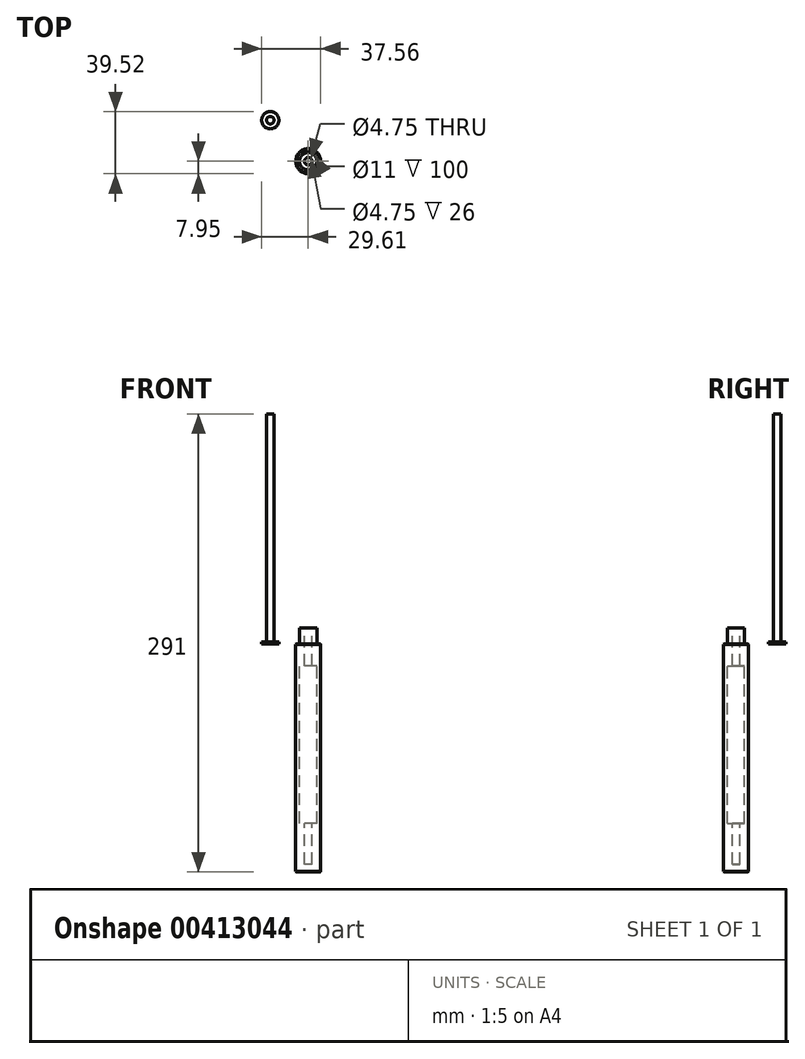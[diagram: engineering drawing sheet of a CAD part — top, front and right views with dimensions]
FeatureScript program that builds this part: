
annotation { "Feature Type Name" : "Feature", "Feature Type Description" : "" }
export const myFeature = defineFeature(function(context is Context, id is Id, definition is map)
    precondition{}
    {
        {
            var Q0;
            Q0=qCreatedBy(makeId("Top.planeOp"),FACE);
            var sketch = newSketch(context, id + "F0", { "sketchPlane" : qUnion([Q0])});
            skCircle(sketch, "E0", {"center": v(0, 0) * mm, "radius": 7.95 * mm});
            skSolve(sketch);
        }
        {
            var Q0;
            Q0=makeQuery(id+"F0.imprint","IMPRINT",FACE,{"disambiguationData":[TD([[makeQuery(id+"F0.imprint","IMPRINT",EDGE,{"derivedFrom":sQuery(id+"F0.wireOp",EDGE,"E0")}),1.0]])]});
            extrude(context, id + "F1", {"entities" : qUnion([Q0]), "oppositeDirection" : true, "depth" : 145 * mm});
        }
        {
            var Q0;
            Q0=makeQuery(id+"F1.opExtrude","CAP_FACE",FACE,{"disambiguationData":[OSD([sQuery(id+"F0.wireOp",EDGE,"E0")])],"isStart":true});
            var sketch = newSketch(context, id + "F2", { "sketchPlane" : qUnion([Q0])});
            skCircle(sketch, "E1", {"center": v(0, 0) * mm, "radius": 5.5 * mm});
            skSolve(sketch);
        }
        {
            var Q0;
            Q0=makeQuery(id+"F2.imprint","IMPRINT",FACE,{"disambiguationData":[TD([[makeQuery(id+"F2.imprint","IMPRINT",EDGE,{"derivedFrom":sQuery(id+"F2.wireOp",EDGE,"E1")}),1.0]])]});
            extrude(context, id + "F3", {"entities" : qUnion([Q0]), "operationType" : NewBodyOperationType.ADD, "depth" : 10 * mm});
        }
        {
            var Q0;
            Q0=makeQuery(id+"F1.opExtrude","CAP_EDGE",EDGE,{"disambiguationData":[OSD([sQuery(id+"F0.wireOp",EDGE,"E0")])],"isStart":true});
            var Q1;
            Q1=makeQuery(id+"F1.opExtrude","CAP_EDGE",EDGE,{"disambiguationData":[OSD([sQuery(id+"F0.wireOp",EDGE,"E0")])],"isStart":false});
            chamfer(context, id + "F4", {"entities" : qUnion([Q0, Q1]), "width" : .5 * mm, "tangentPropagation" : true});
        }
        {
            var Q0;
            Q0=makeQuery(id+"F3.opExtrude","CAP_FACE",FACE,{"disambiguationData":[OSD([sQuery(id+"F2.wireOp",EDGE,"E1")])],"isStart":false});
            var sketch = newSketch(context, id + "F5", { "sketchPlane" : qUnion([Q0])});
            skCircle(sketch, "E2", {"center": v(0, 0) * mm, "radius": 2.38 * mm});
            skSolve(sketch);
        }
        {
            var Q0;
            Q0=makeQuery(id+"F5.imprint","IMPRINT",FACE,{"disambiguationData":[TD([[makeQuery(id+"F5.imprint","IMPRINT",EDGE,{"derivedFrom":sQuery(id+"F5.wireOp",EDGE,"E2")}),1.0]])]});
            extrude(context, id + "F6", {"entities" : qUnion([Q0]), "operationType" : NewBodyOperationType.REMOVE, "oppositeDirection" : true, "depth" : 150 * mm});
        }
        {
            var Q0;
            Q0=makeQuery(id+"F3.opExtrude","CAP_FACE",FACE,{"disambiguationData":[OSD([sQuery(id+"F2.wireOp",EDGE,"E1")])],"isStart":false});
            extrude(context, id + "F7", {"entities" : qUnion([Q0]), "operationType" : NewBodyOperationType.REMOVE, "oppositeDirection" : true, "depth" : 124 * mm, "hasSecondDirection" : true, "secondDirectionOppositeDirection" : true, "secondDirectionDepth" : 24 * mm});
        }
        {
            var Q0;
            Q0=qCreatedBy(makeId("Top.planeOp"),FACE);
            var sketch = newSketch(context, id + "F8", { "sketchPlane" : qUnion([Q0])});
            skCircle(sketch, "E3", {"center": v(-24.1, 26.07) * mm, "radius": 5.5 * mm});
            skSolve(sketch);
        }
        {
            var Q0;
            Q0=makeQuery(id+"F8.imprint","IMPRINT",FACE,{"disambiguationData":[TD([[makeQuery(id+"F8.imprint","IMPRINT",EDGE,{"derivedFrom":sQuery(id+"F8.wireOp",EDGE,"E3")}),1.0]])]});
            extrude(context, id + "F9", {"entities" : qUnion([Q0]), "depth" : 1 * mm});
        }
        {
            var Q0;
            Q0=makeQuery(id+"F9.opExtrude","CAP_FACE",FACE,{"disambiguationData":[OSD([sQuery(id+"F8.wireOp",EDGE,"E3")])],"isStart":false});
            var sketch = newSketch(context, id + "F10", { "sketchPlane" : qUnion([Q0])});
            skCircle(sketch, "E4", {"center": v(-24.1, 26.07) * mm, "radius": 2.38 * mm});
            skSolve(sketch);
        }
        {
            var Q0;
            Q0=makeQuery(id+"F10.imprint","IMPRINT",FACE,{"disambiguationData":[TD([[makeQuery(id+"F10.imprint","IMPRINT",EDGE,{"derivedFrom":sQuery(id+"F10.wireOp",EDGE,"E4")}),1.0]])]});
            extrude(context, id + "F11", {"entities" : qUnion([Q0]), "operationType" : NewBodyOperationType.ADD, "depth" : (113 + 32) * mm});
        }
    });
